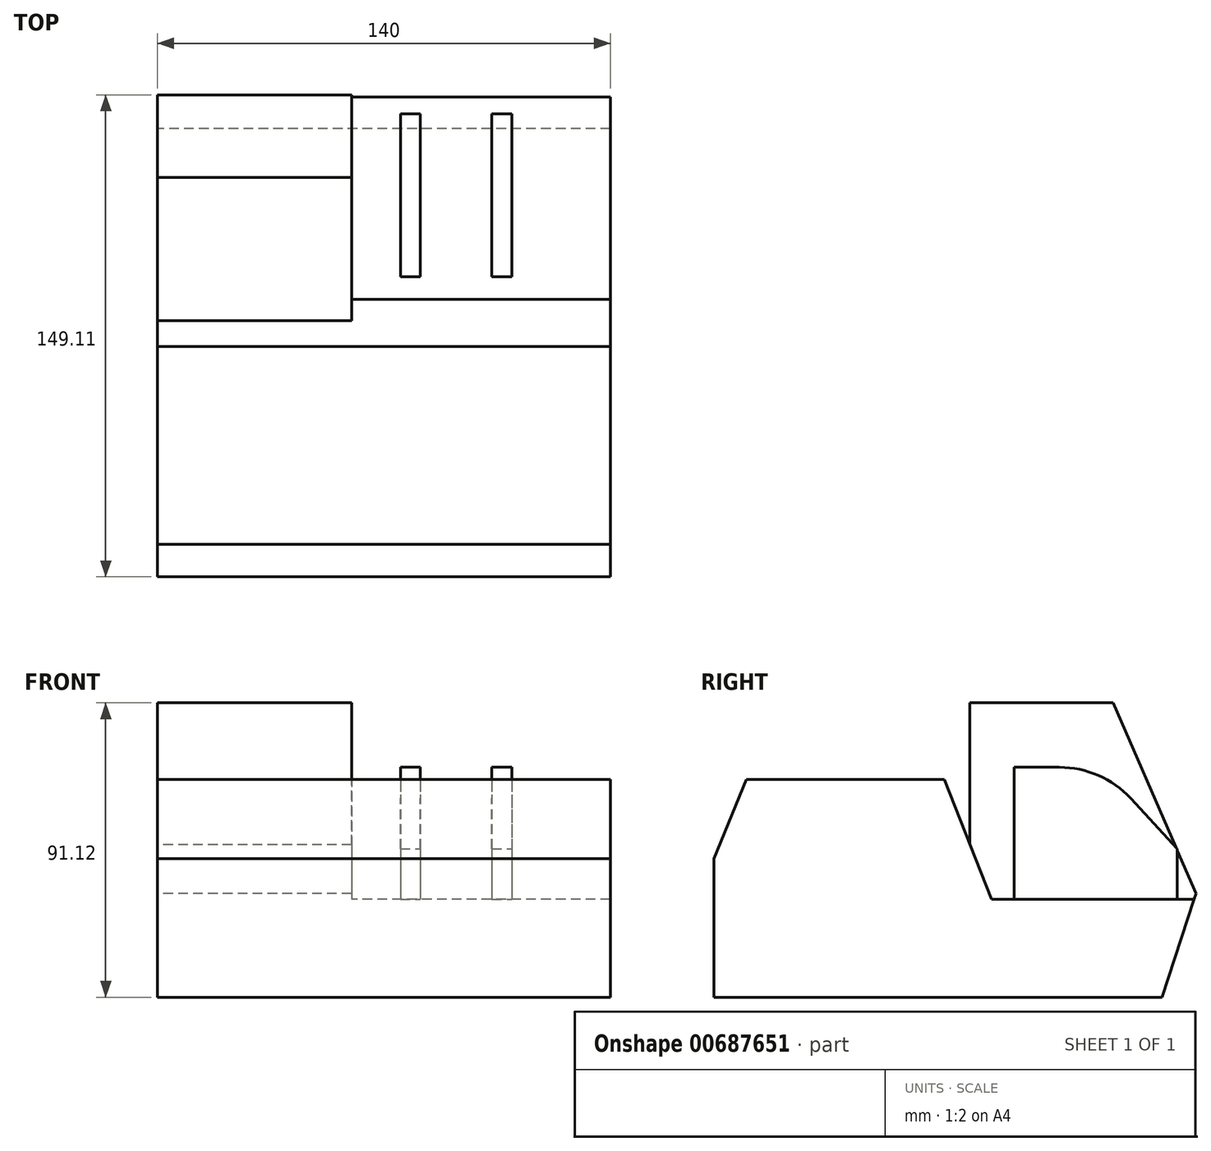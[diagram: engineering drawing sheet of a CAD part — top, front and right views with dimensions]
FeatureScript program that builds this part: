
annotation { "Feature Type Name" : "Feature", "Feature Type Description" : "" }
export const myFeature = defineFeature(function(context is Context, id is Id, definition is map)
    precondition{}
    {
        {
            var Q0;
            Q0=qCreatedBy(makeId("Right.planeOp"),FACE);
            var sketch = newSketch(context, id + "F0", { "sketchPlane" : qUnion([Q0])});
            skLineSegment(sketch, "E0", {"start": v(-95.09, 4) * mm, "end": v(-85, 28.48) * mm});
            skLineSegment(sketch, "E1", {"start": v(-85, 28.48) * mm, "end": v(-23.78, 28.48) * mm});
            skLineSegment(sketch, "E2", {"start": v(-23.78, 28.48) * mm, "end": v(-15.85, 8.31) * mm});
            skLineSegment(sketch, "E3", {"start": v(-15.85, 8.31) * mm, "end": v(-15.85, 52.25) * mm});
            skLineSegment(sketch, "E4", {"start": v(-15.85, 52.25) * mm, "end": v(28.44, 52.25) * mm});
            skLineSegment(sketch, "E5", {"start": v(28.44, 52.25) * mm, "end": v(54.02, -6.81) * mm});
            skLineSegment(sketch, "E6", {"start": v(54.02, -6.81) * mm, "end": v(43.57, -38.87) * mm});
            skLineSegment(sketch, "E7", {"start": v(43.57, -38.87) * mm, "end": v(-95.09, -38.87) * mm});
            skLineSegment(sketch, "E8", {"start": v(-95.09, -38.87) * mm, "end": v(-95.09, 4) * mm});
            skSolve(sketch);
        }
        {
            var Q0;
            Q0=makeQuery(id+"F0.imprint","IMPRINT",FACE,{"disambiguationData":[TD([[makeQuery(id+"F0.imprint","IMPRINT",EDGE,{"derivedFrom":sQuery(id+"F0.wireOp",EDGE,"E0")}),-1.0]])]});
            extrude(context, id + "F1", {"entities" : qUnion([Q0]), "depth" : 60 * mm, "offsetDistance" : 25 * mm});
        }
        {
            var Q0;
            Q0=makeQuery(id+"F1.opExtrude","CAP_FACE",FACE,{"disambiguationData":[OSD([sQuery(id+"F0.wireOp",EDGE,"E0"),sQuery(id+"F0.wireOp",EDGE,"E1"),sQuery(id+"F0.wireOp",EDGE,"E2"),sQuery(id+"F0.wireOp",EDGE,"E3"),sQuery(id+"F0.wireOp",EDGE,"E4"),sQuery(id+"F0.wireOp",EDGE,"E5"),sQuery(id+"F0.wireOp",EDGE,"E6"),sQuery(id+"F0.wireOp",EDGE,"E7"),sQuery(id+"F0.wireOp",EDGE,"E8")])],"isStart":false});
            var sketch = newSketch(context, id + "F2", { "sketchPlane" : qUnion([Q0])});
            skLineSegment(sketch, "E9", {"start": v(-15.85, 8.31) * mm, "end": v(-9.2, -8.6) * mm});
            skLineSegment(sketch, "E10", {"start": v(-9.2, -8.6) * mm, "end": v(53.43, -8.6) * mm});
            skSolve(sketch);
        }
        {
            var Q0;
            Q0=makeQuery(id+"F2.imprint","IMPRINT",FACE,{"disambiguationData":[TD([[makeQuery(id+"F2.imprint","IMPRINT",EDGE,{"derivedFrom":sQuery(id+"F2.wireOp",EDGE,"E9")}),-1.0]])]});
            extrude(context, id + "F3", {"entities" : qUnion([Q0]), "operationType" : NewBodyOperationType.ADD, "depth" : 80 * mm, "offsetDistance" : 25 * mm});
        }
        {
            var Q0;
            Q0=makeQuery(id+"F3.opExtrude","SWEPT_FACE",FACE,{"disambiguationData":[OSD([sQuery(id+"F2.wireOp",EDGE,"E10")])]});
            var sketch = newSketch(context, id + "F4", { "sketchPlane" : qUnion([Q0])});
            skLineSegment(sketch, "E11.bottom", {"start": v(75.13, -2.2) * mm, "end": v(81.24, -2.2) * mm});
            skLineSegment(sketch, "E11.top", {"start": v(75.13, 48.23) * mm, "end": v(81.24, 48.23) * mm});
            skLineSegment(sketch, "E11.left", {"start": v(75.13, -2.2) * mm, "end": v(75.13, 48.23) * mm});
            skLineSegment(sketch, "E11.right", {"start": v(81.24, -2.2) * mm, "end": v(81.24, 48.23) * mm});
            skLineSegment(sketch, "E12.bottom", {"start": v(103.4, -2.2) * mm, "end": v(109.51, -2.2) * mm});
            skLineSegment(sketch, "E12.top", {"start": v(103.4, 48.23) * mm, "end": v(109.51, 48.23) * mm});
            skLineSegment(sketch, "E12.left", {"start": v(103.4, -2.2) * mm, "end": v(103.4, 48.23) * mm});
            skLineSegment(sketch, "E12.right", {"start": v(109.51, -2.2) * mm, "end": v(109.51, 48.23) * mm});
            skSolve(sketch);
        }
        {
            var Q0;
            Q0=makeQuery(id+"F4.imprint","IMPRINT",FACE,{"disambiguationData":[TD([[makeQuery(id+"F4.imprint","IMPRINT",EDGE,{"derivedFrom":sQuery(id+"F4.wireOp",EDGE,"E11.bottom")}),1.0]])]});
            var Q1;
            Q1=makeQuery(id+"F4.imprint","IMPRINT",FACE,{"disambiguationData":[TD([[makeQuery(id+"F4.imprint","IMPRINT",EDGE,{"derivedFrom":sQuery(id+"F4.wireOp",EDGE,"E12.bottom")}),1.0]])]});
            extrude(context, id + "F5", {"entities" : qUnion([Q0, Q1]), "operationType" : NewBodyOperationType.ADD, "depth" : 57.3 * mm, "offsetDistance" : 25 * mm});
        }
        {
            var Q0;
            Q0=makeQuery(id+"F5.opExtrude","SWEPT_FACE",FACE,{"disambiguationData":[OSD([sQuery(id+"F4.wireOp",EDGE,"E12.right")])]});
            var sketch = newSketch(context, id + "F6", { "sketchPlane" : qUnion([Q0])});
            skLineSegment(sketch, "E13", {"start": v(-2.2, 32.27) * mm, "end": v(24.92, 32.27) * mm});
            skLineSegment(sketch, "E14", {"start": v(24.92, 32.27) * mm, "end": v(48.23, 7.06) * mm});
            skSolve(sketch);
        }
        {
            var Q0;
            {var subQ3=sQuery(id+"F6.wireOp",EDGE,"E13");Q0=makeQuery(id+"F6.imprint","IMPRINT",FACE,{"disambiguationData":[TD([[makeQuery(id+"F6.imprint","IMPRINT",EDGE,{"derivedFrom":subQ3}),1.0]])]});}
            extrude(context, id + "F7", {"entities" : qUnion([Q0]), "operationType" : NewBodyOperationType.REMOVE, "oppositeDirection" : true, "depth" : 45.7 * mm, "offsetDistance" : 25 * mm});
        }
        {
            var Q0;
            {var subQ0=sQuery(id+"F4.wireOp",EDGE,"E12.top");var subQ1=sQuery(id+"F6.wireOp",EDGE,"E14");Q0=makeQuery(id+"F7.boolean.opBoolean","COPY",EDGE,{"disambiguationData":[topologyDisambiguationEdgeConnected([makeQuery(id+"F5.opExtrude","SWEPT_FACE",FACE,{"disambiguationData":[OSD([subQ0])]})])],"derivedFrom":makeQuery(id+"F7.opExtrude","SWEPT_EDGE",EDGE,{"disambiguationData":[OSD([subQ0,sQuery(id+"F4.wireOp",EDGE,"E12.right"),subQ1])]})});}
            var Q1;
            {var subQ0=sQuery(id+"F6.wireOp",EDGE,"E13");var subQ1=sQuery(id+"F6.wireOp",EDGE,"E14");Q1=makeQuery(id+"F7.boolean.opBoolean","COPY",EDGE,{"disambiguationData":[TD([makeQuery(id+"F5.opExtrude","SWEPT_FACE",FACE,{"disambiguationData":[OSD([sQuery(id+"F4.wireOp",EDGE,"E12.left")])]})])],"derivedFrom":makeQuery(id+"F7.opExtrude","SWEPT_EDGE",EDGE,{"disambiguationData":[OSD([subQ0,subQ1])]})});}
            var Q2;
            {var subQ0=sQuery(id+"F6.wireOp",EDGE,"E13");var subQ1=sQuery(id+"F6.wireOp",EDGE,"E14");Q2=makeQuery(id+"F7.boolean.opBoolean","COPY",EDGE,{"disambiguationData":[TD([makeQuery(id+"F5.opExtrude","SWEPT_FACE",FACE,{"disambiguationData":[OSD([sQuery(id+"F4.wireOp",EDGE,"E11.left")])]})])],"derivedFrom":makeQuery(id+"F7.opExtrude","SWEPT_EDGE",EDGE,{"disambiguationData":[OSD([subQ0,subQ1])]})});}
            var Q3;
            {var subQ0=sQuery(id+"F6.wireOp",EDGE,"E14");Q3=makeQuery(id+"F7.boolean.opBoolean","COPY",EDGE,{"disambiguationData":[topologyDisambiguationEdgeConnected([makeQuery(id+"F5.opExtrude","SWEPT_FACE",FACE,{"disambiguationData":[OSD([sQuery(id+"F4.wireOp",EDGE,"E11.top")])]})])],"derivedFrom":makeQuery(id+"F7.opExtrude","SWEPT_EDGE",EDGE,{"disambiguationData":[OSD([sQuery(id+"F4.wireOp",EDGE,"E12.top"),sQuery(id+"F4.wireOp",EDGE,"E12.right"),subQ0])]})});}
            fillet(context, id + "F8", {"entities" : qUnion([Q0, Q1, Q2, Q3]), "radius" : 30 * mm, "tangentPropagation" : true, "allowEdgeOverflow" : false});
        }
    });
